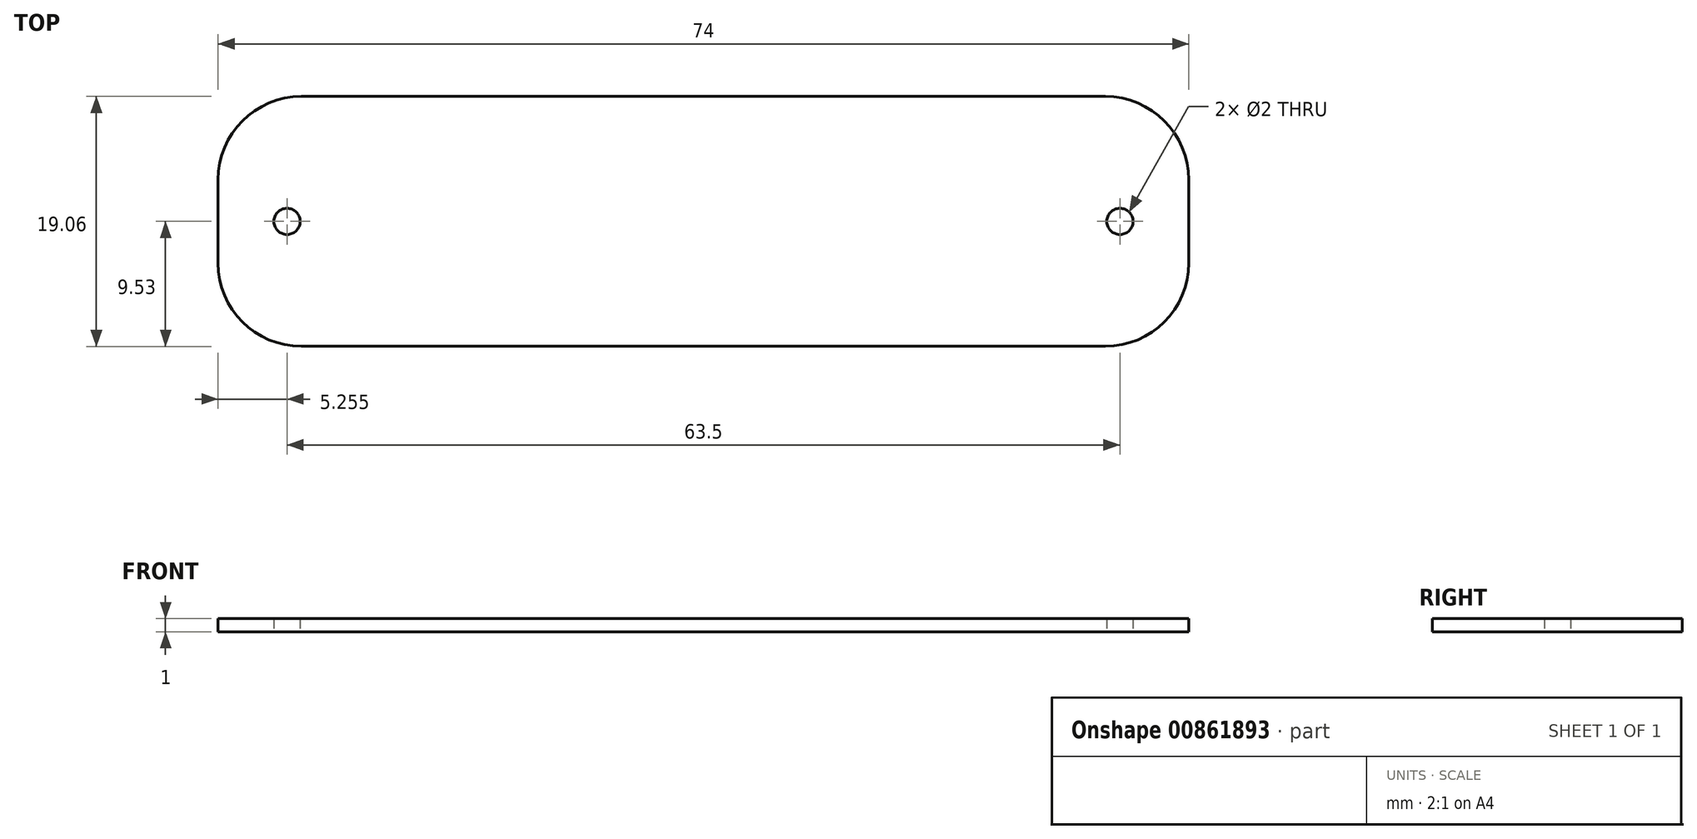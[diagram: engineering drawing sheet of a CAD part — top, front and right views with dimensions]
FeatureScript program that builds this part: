
annotation { "Feature Type Name" : "Feature", "Feature Type Description" : "" }
export const myFeature = defineFeature(function(context is Context, id is Id, definition is map)
    precondition{}
    {
        {
            var Q0;
            Q0=qCreatedBy(makeId("Top.planeOp"),FACE);
            var sketch = newSketch(context, id + "F0", { "sketchPlane" : qUnion([Q0])});
            skLineSegment(sketch, "E0.bottom", {"start": v(30.65, -9.52) * mm, "end": v(-30.65, -9.53) * mm});
            skLineSegment(sketch, "E0.top", {"start": v(30.65, 9.53) * mm, "end": v(-30.65, 9.52) * mm});
            skLineSegment(sketch, "E0.left", {"start": v(37, -3.17) * mm, "end": v(37, 3.18) * mm});
            skLineSegment(sketch, "E0.right", {"start": v(-37, -3.18) * mm, "end": v(-37, 3.17) * mm});
            skPoint(sketch, "E0.middle", {"position": v(0, 0) * mm});
            skCircle(sketch, "E1", {"center": v(-31.75, 0) * mm, "radius": 1 * mm});
            skCircle(sketch, "E2", {"center": v(31.75, 0) * mm, "radius": 1 * mm});
            skPoint(sketch, "E3.visualSharp", {"position": v(-37, 9.52) * mm});
            skArc(sketch, "E3.filletArc", {"start": v(-30.65, 9.52) * mm, "mid": v(-35.14, 7.67) * mm, "end": v(-37, 3.17) * mm});
            skPoint(sketch, "E4.visualSharp", {"position": v(-37, -9.53) * mm});
            skArc(sketch, "E4.filletArc", {"start": v(-37, -3.18) * mm, "mid": v(-35.14, -7.67) * mm, "end": v(-30.65, -9.53) * mm});
            skPoint(sketch, "E5.visualSharp", {"position": v(37, 9.53) * mm});
            skArc(sketch, "E5.filletArc", {"start": v(37, 3.18) * mm, "mid": v(35.14, 7.67) * mm, "end": v(30.65, 9.53) * mm});
            skPoint(sketch, "E6.visualSharp", {"position": v(37, -9.52) * mm});
            skArc(sketch, "E6.filletArc", {"start": v(30.65, -9.52) * mm, "mid": v(35.14, -7.67) * mm, "end": v(37, -3.17) * mm});
            skSolve(sketch);
        }
        {
            var Q0;
            Q0=makeQuery(id+"F0.imprint","IMPRINT",FACE,{"disambiguationData":[TD([[makeQuery(id+"F0.imprint","IMPRINT",EDGE,{"derivedFrom":sQuery(id+"F0.wireOp",EDGE,"E0.bottom")}),-1.0]])]});
            extrude(context, id + "F1", {"entities" : qUnion([Q0]), "endBound" : BoundingType.SYMMETRIC, "depth" : 1 * mm, "offsetDistance" : 25.4 * mm});
        }
    });
